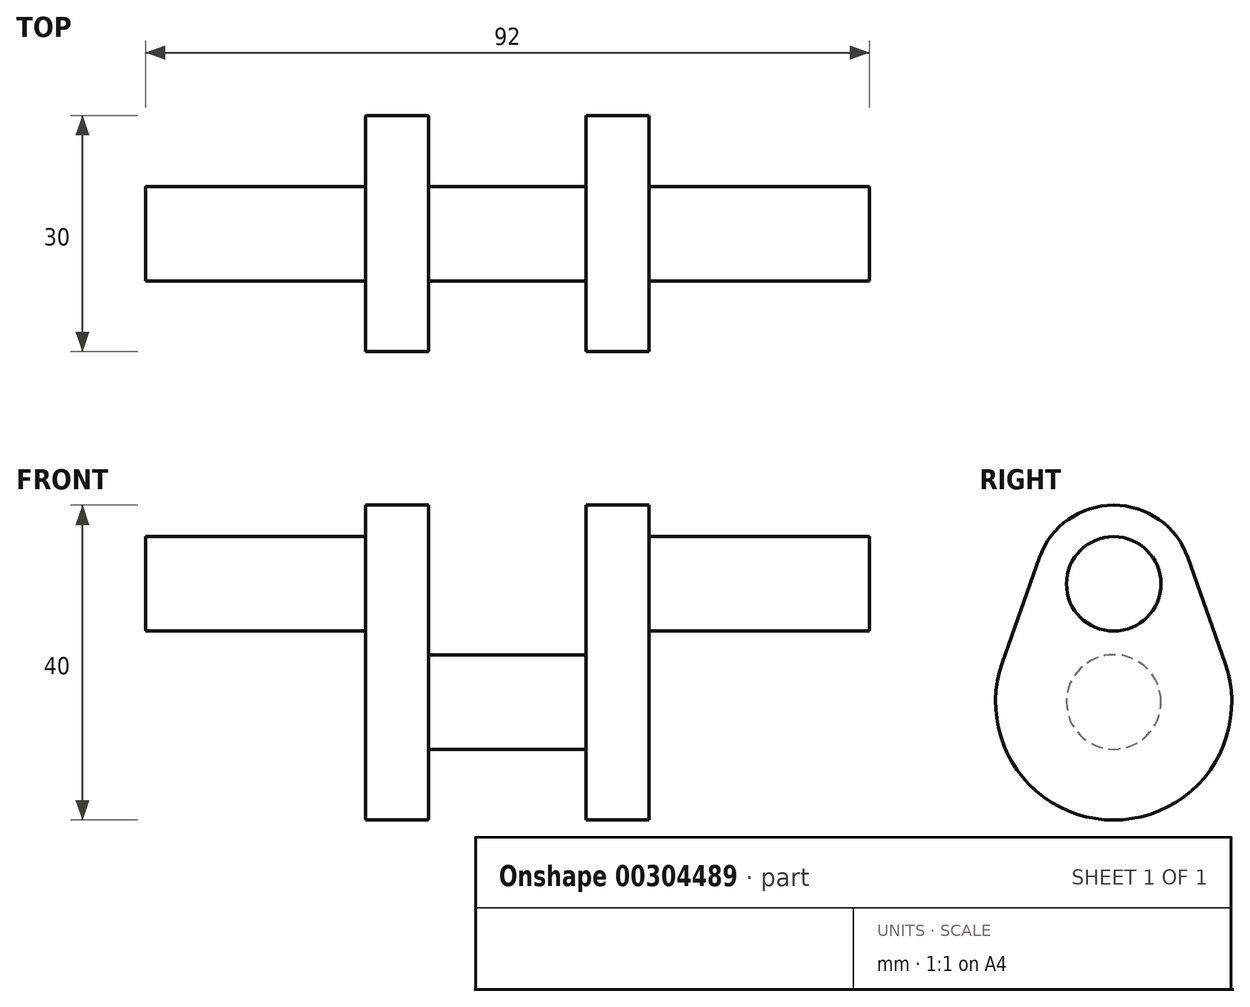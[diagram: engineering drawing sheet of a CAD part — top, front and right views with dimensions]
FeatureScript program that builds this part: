
annotation { "Feature Type Name" : "Feature", "Feature Type Description" : "" }
export const myFeature = defineFeature(function(context is Context, id is Id, definition is map)
    precondition{}
    {
        {
            var Q0;
            Q0=qCreatedBy(makeId("Right.planeOp"),FACE);
            var sketch = newSketch(context, id + "F0", { "sketchPlane" : qUnion([Q0])});
            skArc(sketch, "E0", {"start": v(-14.14, 5) * mm, "mid": v(0, -15) * mm, "end": v(14.14, 5) * mm});
            skLineSegment(sketch, "E1", {"start": v(0, 0) * mm, "end": v(0, 25) * mm, "construction": true});
            skArc(sketch, "E2", {"start": v(9.43, 18.33) * mm, "mid": v(0, 25) * mm, "end": v(-9.43, 18.33) * mm});
            skLineSegment(sketch, "E3", {"start": v(-14.14, 5) * mm, "end": v(-9.43, 18.33) * mm});
            skLineSegment(sketch, "E4.MirrorCS", {"start": v(14.14, 5) * mm, "end": v(9.43, 18.33) * mm});
            skCircle(sketch, "E5", {"center": v(0, 0) * mm, "radius": 6 * mm});
            skSolve(sketch);
        }
        {
            var Q0;
            Q0=makeQuery(id+"F0.imprint","IMPRINT",FACE,{"disambiguationData":[TD([[makeQuery(id+"F0.imprint","IMPRINT",EDGE,{"derivedFrom":sQuery(id+"F0.wireOp",EDGE,"E0")}),1.0]])]});
            var Q1;
            Q1=makeQuery(id+"F0.imprint","IMPRINT",FACE,{"disambiguationData":[TD([[makeQuery(id+"F0.imprint","IMPRINT",EDGE,{"derivedFrom":sQuery(id+"F0.wireOp",EDGE,"E5")}),1.0]])]});
            extrude(context, id + "F1", {"entities" : qUnion([Q0, Q1]), "depth" : 8 * mm});
        }
        {
            var Q0;
            Q0=makeQuery(id+"F0.imprint","IMPRINT",FACE,{"disambiguationData":[TD([[makeQuery(id+"F0.imprint","IMPRINT",EDGE,{"derivedFrom":sQuery(id+"F0.wireOp",EDGE,"E5")}),1.0]])]});
            extrude(context, id + "F2", {"entities" : qUnion([Q0]), "operationType" : NewBodyOperationType.ADD, "oppositeDirection" : true, "depth" : 10 * mm});
        }
        {
            var Q0;
            Q0=makeQuery(id+"F1.opExtrude","CAP_FACE",FACE,{"disambiguationData":[OSD([sQuery(id+"F0.wireOp",EDGE,"E0"),sQuery(id+"F0.wireOp",EDGE,"E2"),sQuery(id+"F0.wireOp",EDGE,"E3"),sQuery(id+"F0.wireOp",EDGE,"E4.MirrorCS")])],"isStart":false});
            var sketch = newSketch(context, id + "F3", { "sketchPlane" : qUnion([Q0])});
            skCircle(sketch, "E6", {"center": v(0, 15) * mm, "radius": 6 * mm});
            skSolve(sketch);
        }
        {
            var Q0;
            Q0=makeQuery(id+"F3.imprint","IMPRINT",FACE,{"disambiguationData":[TD([[makeQuery(id+"F3.imprint","IMPRINT",EDGE,{"derivedFrom":sQuery(id+"F3.wireOp",EDGE,"E6")}),1.0]])]});
            extrude(context, id + "F4", {"entities" : qUnion([Q0]), "operationType" : NewBodyOperationType.ADD, "depth" : 20 * mm});
        }
        {
            var Q0;
            Q0=qCreatedBy(makeId("Right.planeOp"),FACE);
            cPlane(context, id + "F5", {"entities" : qUnion([Q0]), "cplaneType" : CPlaneType.OFFSET, "offset" : 10 * mm, "oppositeDirection" : true, "width" : 150 * mm, "height" : 150 * mm});
        }
        {
            var Q0;
            Q0=makeQuery(id+"F1.opExtrude","SWEPT_BODY",BODY,{"disambiguationData":[OSD([sQuery(id+"F0.wireOp",EDGE,"E0"),sQuery(id+"F0.wireOp",EDGE,"E2"),sQuery(id+"F0.wireOp",EDGE,"E3"),sQuery(id+"F0.wireOp",EDGE,"E4.MirrorCS")])]});
            var Q1;
            Q1=qCreatedBy(id+"F5.planeOp",FACE);
            mirror(context, id + "F6", {"operationType" : NewBodyOperationType.ADD, "entities" : qUnion([Q0]), "mirrorPlane" : qUnion([Q1])});
        }
        {
            var Q0;
            Q0=makeQuery(id+"F4.opExtrude","CAP_FACE",FACE,{"disambiguationData":[OSD([sQuery(id+"F3.wireOp",EDGE,"E6")])],"isStart":false});
            extrude(context, id + "F7", {"entities" : qUnion([Q0]), "operationType" : NewBodyOperationType.ADD, "depth" : 8 * mm});
        }
        {
            var Q0;
            Q0=makeQuery(id+"F6.opPattern","COPY",FACE,{"derivedFrom":makeQuery(id+"F4.opExtrude","CAP_FACE",FACE,{"disambiguationData":[OSD([sQuery(id+"F3.wireOp",EDGE,"E6")])],"isStart":false}),"instanceName":"1"});
            extrude(context, id + "F8", {"entities" : qUnion([Q0]), "operationType" : NewBodyOperationType.ADD, "depth" : 8 * mm});
        }
    });
